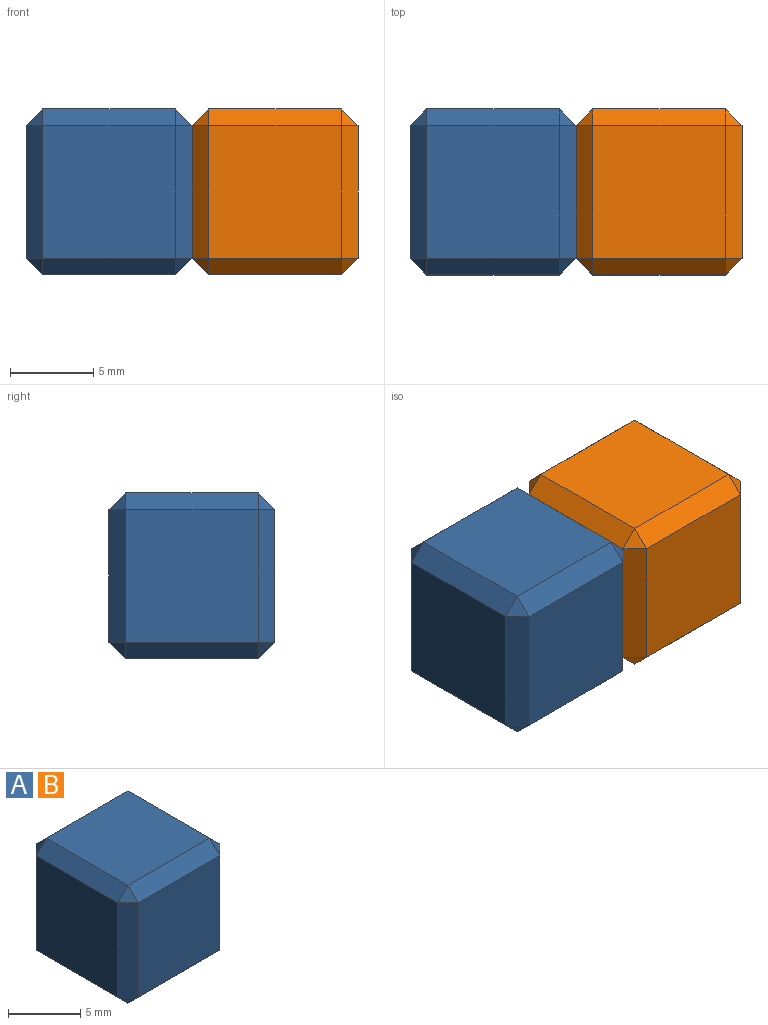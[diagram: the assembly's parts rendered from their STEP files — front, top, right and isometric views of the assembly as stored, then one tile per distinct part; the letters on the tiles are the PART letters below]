
ASSEMBLY  parts=2 mates=1
PART A: 26 faces, bbox 10x10x10 mm
  f0: plane 8x8mm, normal (1,0,0), area 64mm2, adj f11,f20,f21,f25
  f1: plane 8x8mm, normal (0,1,0), area 64mm2, adj f6,f10,f11,f12
  f2: plane 8x8mm, normal (-1,0,0), area 64mm2, adj f6,f9,f13,f14
  f3: plane 8x8mm, normal (0,-1,0), area 64mm2, adj f14,f19,f22,f25
  f4: plane 8x8mm, normal (0,0,1), area 64mm2, adj f9,f10,f19,f20
  f5: plane 8x8mm, normal (0,0,-1), area 64mm2, adj f12,f13,f21,f22
  f6: plane 8x1mm, normal (-0.71,0.71,0), area 11.3mm2, adj f1,f2,f7,f8
  f7: plane 1x1mm, normal (-0.58,0.58,0.58), area 0.9mm2, adj f6,f9,f10
  f8: plane 1x1mm, normal (-0.58,0.58,-0.58), area 0.9mm2, adj f6,f12,f13
  f9: plane 8x1mm, normal (-0.71,0,0.71), area 11.3mm2, adj f2,f4,f7,f15
  f10: plane 8x1mm, normal (0,0.71,0.71), area 11.3mm2, adj f1,f4,f7,f16
  f11: plane 8x1mm, normal (0.71,0.71,0), area 11.3mm2, adj f0,f1,f16,f17
  f12: plane 8x1mm, normal (0,0.71,-0.71), area 11.3mm2, adj f1,f5,f8,f17
  f13: plane 8x1mm, normal (-0.71,0,-0.71), area 11.3mm2, adj f2,f5,f8,f18
  f14: plane 8x1mm, normal (-0.71,-0.71,0), area 11.3mm2, adj f2,f3,f15,f18
  f15: plane 1x1mm, normal (-0.58,-0.58,0.58), area 0.9mm2, adj f9,f14,f19
  f16: plane 1x1mm, normal (0.58,0.58,0.58), area 0.9mm2, adj f10,f11,f20
  f17: plane 1x1mm, normal (0.58,0.58,-0.58), area 0.9mm2, adj f11,f12,f21
  f18: plane 1x1mm, normal (-0.58,-0.58,-0.58), area 0.9mm2, adj f13,f14,f22
  f19: plane 8x1mm, normal (0,-0.71,0.71), area 11.3mm2, adj f3,f4,f15,f23
  f20: plane 8x1mm, normal (0.71,0,0.71), area 11.3mm2, adj f0,f4,f16,f23
  f21: plane 8x1mm, normal (0.71,0,-0.71), area 11.3mm2, adj f0,f5,f17,f24
  f22: plane 8x1mm, normal (0,-0.71,-0.71), area 11.3mm2, adj f3,f5,f18,f24
  f23: plane 1x1mm, normal (0.58,-0.58,0.58), area 0.9mm2, adj f19,f20,f25
  f24: plane 1x1mm, normal (0.58,-0.58,-0.58), area 0.9mm2, adj f21,f22,f25
  f25: plane 8x1mm, normal (0.71,-0.71,0), area 11.3mm2, adj f0,f3,f23,f24
PART B: same geometry as A
PLACE A t=(-8.39,-1.29,0.33)mm
PLACE B t=(1.61,-1.29,0.33)mm
MATE fastened B.f2 <-> A.f0  axis (-1,0,0) through (-3.39,-1.29,5.33)mm
